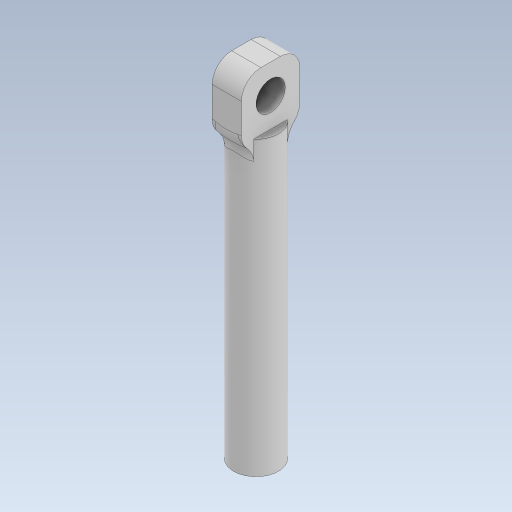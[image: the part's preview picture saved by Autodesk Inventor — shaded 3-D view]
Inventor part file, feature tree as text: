
AUTODESK INVENTOR PART (.ipt)
format: ipt  version: 2023.5 (Build 275446000, 446)  size: 490,496 bytes
history: native  units: mm
features: extrude x3, sketch x2, fillet x1
ambient origin geometry x8: Origin, YZ Plane, XZ Plane, XY Plane, X Axis, Y Axis, Z Axis, Center Point
bodies: Solid1 (feature_tree)
feature tree (6):
  sketch  "Sketch1"  dims[d0=4.6mm d1=6.0mm d2=0.0mm]
  extrude  "Extrusion1"  Depth=6.0mm TaperAngle=0.0deg
  extrude  "Extrusion2"  Depth=3.0mm
  extrude  "Extrusion3"  Depth=20.0mm TaperAngle=0.0deg
  fillet  "Fillet1"  Radius=2.0mm
  sketch  "Sketch2"  dims[d3=30.0mm d4=0.0mm d5=3.0mm d6=20.0mm d7=0.0mm d8=2.0mm d9=6.0mm d10=3.0mm]
